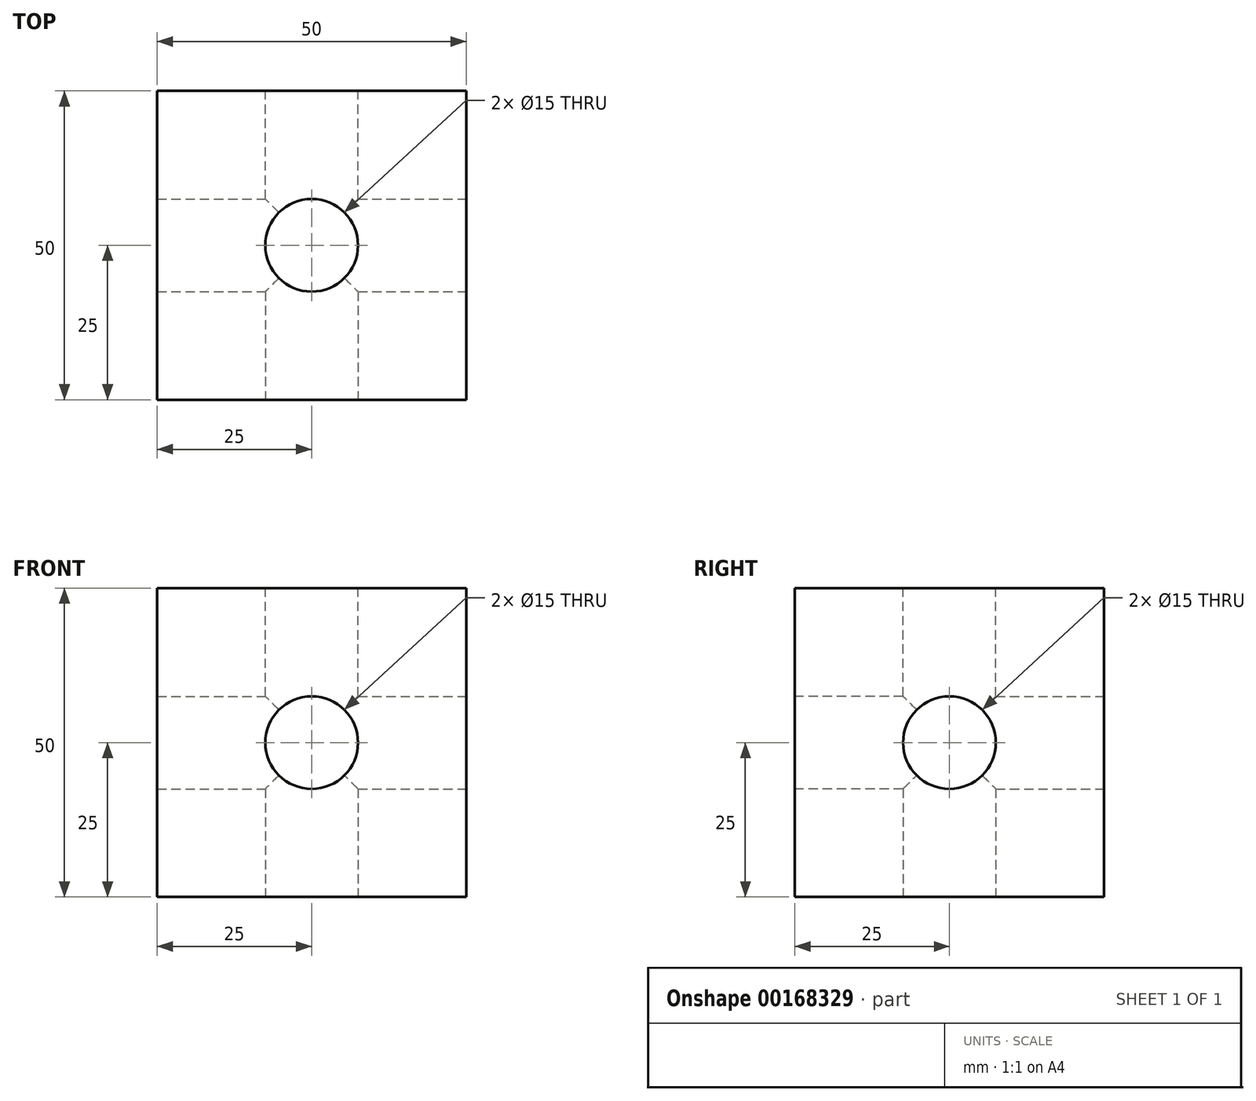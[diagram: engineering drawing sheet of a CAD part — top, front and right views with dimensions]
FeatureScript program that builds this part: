
annotation { "Feature Type Name" : "Feature", "Feature Type Description" : "" }
export const myFeature = defineFeature(function(context is Context, id is Id, definition is map)
    precondition{}
    {
        {
            var Q0;
            Q0=qCreatedBy(makeId("Top.planeOp"),FACE);
            var sketch = newSketch(context, id + "F0", { "sketchPlane" : qUnion([Q0])});
            skLineSegment(sketch, "E0.bottom", {"start": v(25, 25) * mm, "end": v(-25, 25) * mm});
            skLineSegment(sketch, "E0.top", {"start": v(25, -25) * mm, "end": v(-25, -25) * mm});
            skLineSegment(sketch, "E0.left", {"start": v(25, 25) * mm, "end": v(25, -25) * mm});
            skLineSegment(sketch, "E0.right", {"start": v(-25, 25) * mm, "end": v(-25, -25) * mm});
            skPoint(sketch, "E0.middle", {"position": v(0, 0) * mm});
            skSolve(sketch);
        }
        {
            var Q0;
            Q0 = qSketchRegion(id + "F0", true);
            extrude(context, id + "F1", {"entities" : qUnion([Q0]), "depth" : 50 * mm});
        }
        {
            var Q0;
            Q0=makeQuery(id+"F1.opExtrude","CAP_FACE",FACE,{"disambiguationData":[OSD([sQuery(id+"F0.wireOp",EDGE,"E0.bottom"),sQuery(id+"F0.wireOp",EDGE,"E0.top"),sQuery(id+"F0.wireOp",EDGE,"E0.left"),sQuery(id+"F0.wireOp",EDGE,"E0.right")])],"isStart":false});
            var sketch = newSketch(context, id + "F2", { "sketchPlane" : qUnion([Q0])});
            skCircle(sketch, "E1", {"center": v(0, 0) * mm, "radius": 7.5 * mm});
            skSolve(sketch);
        }
        {
            var Q0;
            Q0=makeQuery(id+"F1.opExtrude","SWEPT_FACE",FACE,{"disambiguationData":[OSD([sQuery(id+"F0.wireOp",EDGE,"E0.left")])]});
            var sketch = newSketch(context, id + "F3", { "sketchPlane" : qUnion([Q0])});
            skCircle(sketch, "E2", {"center": v(0, 25) * mm, "radius": 7.5 * mm});
            skPoint(sketch, "E2.centerSnap0", {"position": v(25, 25) * mm});
            skSolve(sketch);
        }
        {
            var Q0;
            Q0=makeQuery(id+"F1.opExtrude","SWEPT_FACE",FACE,{"disambiguationData":[OSD([sQuery(id+"F0.wireOp",EDGE,"E0.top")])]});
            var sketch = newSketch(context, id + "F4", { "sketchPlane" : qUnion([Q0])});
            skCircle(sketch, "E3", {"center": v(0, 25) * mm, "radius": 7.5 * mm});
            skPoint(sketch, "E3.centerSnap0", {"position": v(25, 25) * mm});
            skSolve(sketch);
        }
        {
            var Q0;
            Q0=makeQuery(id+"F1.opExtrude","SWEPT_FACE",FACE,{"disambiguationData":[OSD([sQuery(id+"F0.wireOp",EDGE,"E0.right")])]});
            var sketch = newSketch(context, id + "F5", { "sketchPlane" : qUnion([Q0])});
            skCircle(sketch, "E4", {"center": v(0, 25) * mm, "radius": 7.5 * mm});
            skPoint(sketch, "E4.centerSnap0", {"position": v(25, 25) * mm});
            skSolve(sketch);
        }
        {
            var Q0;
            Q0=makeQuery(id+"F1.opExtrude","SWEPT_FACE",FACE,{"disambiguationData":[OSD([sQuery(id+"F0.wireOp",EDGE,"E0.bottom")])]});
            var sketch = newSketch(context, id + "F6", { "sketchPlane" : qUnion([Q0])});
            skCircle(sketch, "E5", {"center": v(0, 25) * mm, "radius": 7.5 * mm});
            skPoint(sketch, "E5.centerSnap0", {"position": v(25, 25) * mm});
            skSolve(sketch);
        }
        {
            var Q0;
            Q0=makeQuery(id+"F0.imprint","IMPRINT",FACE,{"disambiguationData":[TD([[makeQuery(id+"F0.imprint","IMPRINT",EDGE,{"derivedFrom":sQuery(id+"F0.wireOp",EDGE,"E0.bottom")}),1.0]])]});
            var sketch = newSketch(context, id + "F7", { "sketchPlane" : qUnion([Q0])});
            skCircle(sketch, "E6", {"center": v(0, 0) * mm, "radius": 7.5 * mm});
            skSolve(sketch);
        }
        {
            var Q0;
            Q0 = qSketchRegion(id + "F2", true);
            extrude(context, id + "F8", {"entities" : qUnion([Q0]), "operationType" : NewBodyOperationType.REMOVE, "oppositeDirection" : true, "depth" : 25 * mm});
        }
        {
            var Q0;
            Q0 = qSketchRegion(id + "F3", true);
            extrude(context, id + "F9", {"entities" : qUnion([Q0]), "operationType" : NewBodyOperationType.REMOVE, "oppositeDirection" : true, "depth" : 25 * mm});
        }
        {
            var Q0;
            Q0 = qSketchRegion(id + "F4", true);
            extrude(context, id + "F10", {"entities" : qUnion([Q0]), "operationType" : NewBodyOperationType.REMOVE, "oppositeDirection" : true, "depth" : 25 * mm});
        }
        {
            var Q0;
            Q0 = qSketchRegion(id + "F5", true);
            extrude(context, id + "F11", {"entities" : qUnion([Q0]), "operationType" : NewBodyOperationType.REMOVE, "oppositeDirection" : true, "depth" : 25 * mm});
        }
        {
            var Q0;
            Q0 = qSketchRegion(id + "F6", true);
            extrude(context, id + "F12", {"entities" : qUnion([Q0]), "operationType" : NewBodyOperationType.REMOVE, "oppositeDirection" : true, "depth" : 25 * mm});
        }
        {
            var Q0;
            Q0 = qSketchRegion(id + "F7", true);
            extrude(context, id + "F13", {"entities" : qUnion([Q0]), "operationType" : NewBodyOperationType.REMOVE, "depth" : 25 * mm});
        }
    });
